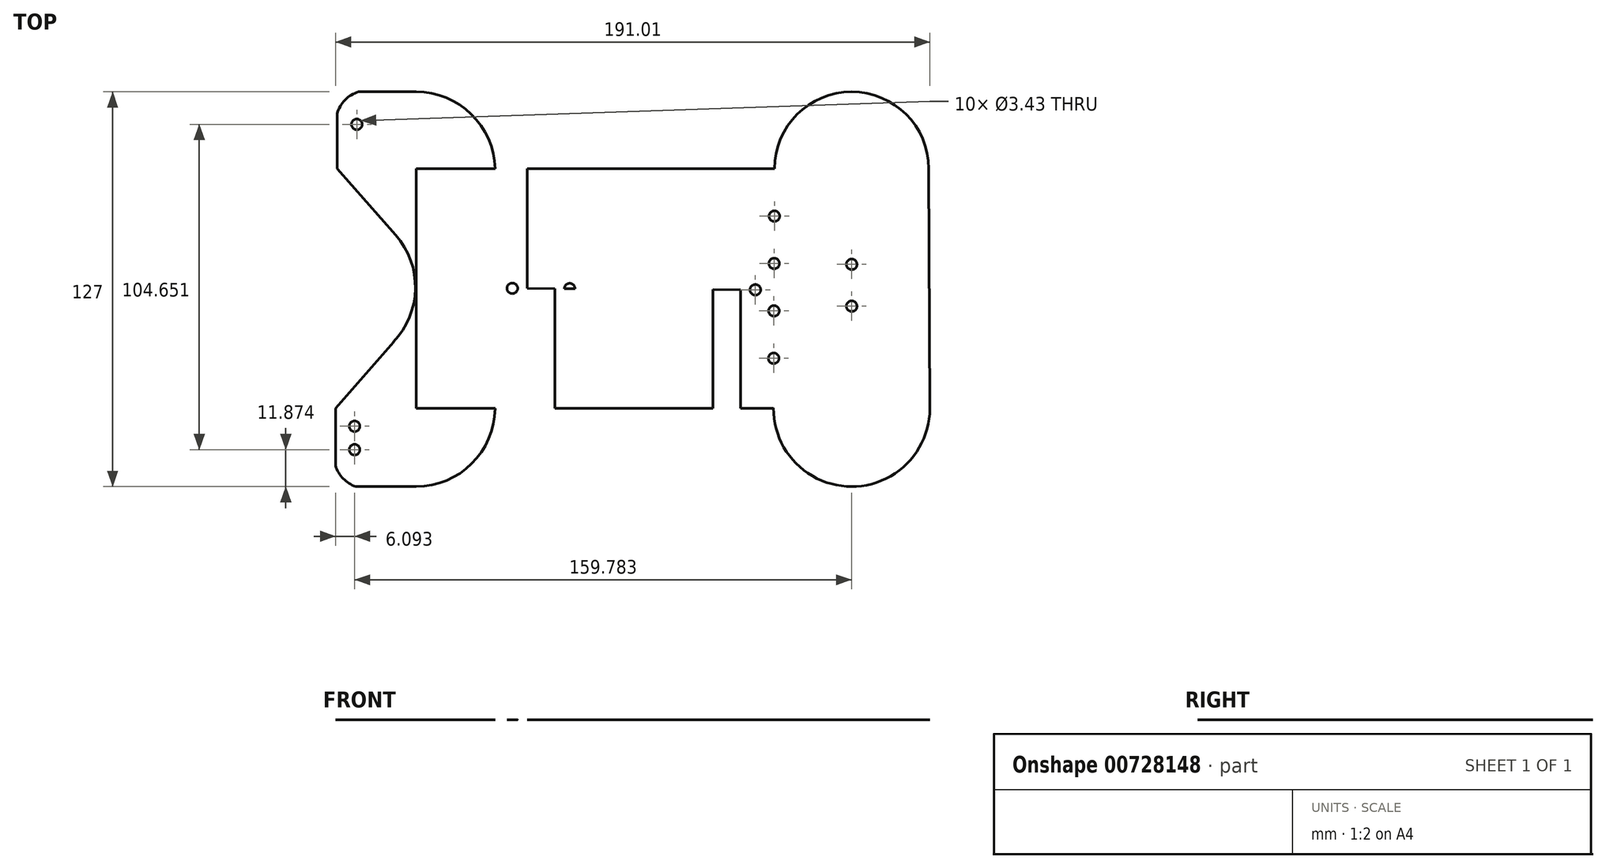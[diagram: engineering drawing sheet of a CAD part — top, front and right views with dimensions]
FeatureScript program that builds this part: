
annotation { "Feature Type Name" : "Feature", "Feature Type Description" : "" }
export const myFeature = defineFeature(function(context is Context, id is Id, definition is map)
    precondition{}
    {
        {
            var Q0;
            Q0=qCreatedBy(makeId("Top.planeOp"),FACE);
            var sketch = newSketch(context, id + "F0", { "sketchPlane" : qUnion([Q0])});
            skLineSegment(sketch, "E0", {"start": v(-83.81, 55.67) * mm, "end": v(-83.81, -21.44) * mm});
            skLineSegment(sketch, "E1", {"start": v(-83.81, 55.67) * mm, "end": v(56.19, 55.67) * mm});
            skCircle(sketch, "E2", {"center": v(56.19, 55.67) * mm, "radius": 24.77 * mm});
            skLineSegment(sketch, "E3", {"start": v(56.19, 55.67) * mm, "end": v(56.19, -21.44) * mm});
            skLineSegment(sketch, "E4", {"start": v(56.19, -21.44) * mm, "end": v(-83.81, -21.44) * mm});
            skCircle(sketch, "E5", {"center": v(56.19, -21.44) * mm, "radius": 25.13 * mm});
            skLineSegment(sketch, "E6", {"start": v(-83.81, 55.67) * mm, "end": v(-83.81, 80.43) * mm});
            skLineSegment(sketch, "E7", {"start": v(-83.81, -21.44) * mm, "end": v(-83.81, -46.57) * mm});
            skLineSegment(sketch, "E8", {"start": v(-83.81, 55.67) * mm, "end": v(-109.21, 55.67) * mm});
            skLineSegment(sketch, "E9", {"start": v(-83.81, -21.44) * mm, "end": v(-109.7, -21.44) * mm});
            skLineSegment(sketch, "E10", {"start": v(56.19, 55.67) * mm, "end": v(56.19, 80.43) * mm});
            skLineSegment(sketch, "E11", {"start": v(56.19, 55.67) * mm, "end": v(80.95, 55.67) * mm});
            skLineSegment(sketch, "E12", {"start": v(56.19, -21.44) * mm, "end": v(81.32, -21.44) * mm});
            skLineSegment(sketch, "E13", {"start": v(56.19, -21.44) * mm, "end": v(56.19, -46.57) * mm});
            skLineSegment(sketch, "E14", {"start": v(-109.21, 55.67) * mm, "end": v(-109.7, -21.44) * mm});
            skLineSegment(sketch, "E15", {"start": v(-83.81, 80.43) * mm, "end": v(56.19, 80.43) * mm});
            skLineSegment(sketch, "E16", {"start": v(80.95, 55.67) * mm, "end": v(81.32, -21.44) * mm});
            skLineSegment(sketch, "E17", {"start": v(-83.81, -46.57) * mm, "end": v(56.19, -46.57) * mm});
            skLineSegment(sketch, "E18", {"start": v(-51.92, 55.67) * mm, "end": v(24.28, 55.67) * mm});
            skLineSegment(sketch, "E19", {"start": v(-51.92, 55.67) * mm, "end": v(-58.42, 55.67) * mm});
            skLineSegment(sketch, "E20", {"start": v(-48.1, 55.67) * mm, "end": v(20.47, 55.67) * mm});
            skLineSegment(sketch, "E21.bottom", {"start": v(-48.1, 55.67) * mm, "end": v(-39.22, 55.67) * mm});
            skLineSegment(sketch, "E21.top", {"start": v(-48.1, -21.44) * mm, "end": v(-39.22, -21.44) * mm});
            skLineSegment(sketch, "E21.left", {"start": v(-48.1, 55.67) * mm, "end": v(-48.1, -21.44) * mm});
            skLineSegment(sketch, "E21.right", {"start": v(-39.22, 55.67) * mm, "end": v(-39.22, -21.44) * mm});
            skLineSegment(sketch, "E22.bottom", {"start": v(20.47, 55.67) * mm, "end": v(11.58, 55.67) * mm});
            skLineSegment(sketch, "E22.top", {"start": v(20.47, -21.44) * mm, "end": v(11.58, -21.44) * mm});
            skLineSegment(sketch, "E22.left", {"start": v(20.47, 55.67) * mm, "end": v(20.47, -21.44) * mm});
            skLineSegment(sketch, "E22.right", {"start": v(11.58, 55.67) * mm, "end": v(11.58, -21.44) * mm});
            skLineSegment(sketch, "E23", {"start": v(-109.45, 17.57) * mm, "end": v(81.14, 16.38) * mm});
            skCircle(sketch, "E24", {"center": v(-52.88, 17.22) * mm, "radius": 1.71 * mm});
            skCircle(sketch, "E25", {"center": v(-34.44, 17.1) * mm, "radius": 1.71 * mm});
            skCircle(sketch, "E26", {"center": v(6.8, 16.84) * mm, "radius": 1.71 * mm});
            skCircle(sketch, "E27", {"center": v(25.23, 16.73) * mm, "radius": 1.71 * mm});
            skLineSegment(sketch, "E28", {"start": v(56.19, 30.9) * mm, "end": v(56.19, 3.7) * mm});
            skCircle(sketch, "E29", {"center": v(56.19, 24.93) * mm, "radius": 1.71 * mm});
            skCircle(sketch, "E30", {"center": v(56.19, 11.47) * mm, "radius": 1.71 * mm});
            skCircle(sketch, "E31", {"center": v(-109.45, 17.57) * mm, "radius": 25.4 * mm});
            skLineSegment(sketch, "E32", {"start": v(-109.21, 55.67) * mm, "end": v(-90.41, 34.38) * mm});
            skLineSegment(sketch, "E33", {"start": v(-109.7, -21.44) * mm, "end": v(-91.07, 0) * mm});
            skLineSegment(sketch, "E34", {"start": v(-96.51, 55.67) * mm, "end": v(-102.86, 55.67) * mm});
            skLineSegment(sketch, "E35.bottom", {"start": v(-109.7, -21.44) * mm, "end": v(-83.81, -21.44) * mm});
            skLineSegment(sketch, "E35.top", {"start": v(-109.7, -46.57) * mm, "end": v(-83.81, -46.57) * mm});
            skLineSegment(sketch, "E35.left", {"start": v(-109.7, -21.44) * mm, "end": v(-109.7, -46.57) * mm});
            skLineSegment(sketch, "E36.bottom", {"start": v(-83.81, 80.43) * mm, "end": v(-109.21, 80.43) * mm});
            skLineSegment(sketch, "E36.left", {"start": v(-83.81, 80.43) * mm, "end": v(-83.81, 55.67) * mm});
            skLineSegment(sketch, "E36.right", {"start": v(-109.21, 80.43) * mm, "end": v(-109.21, 55.67) * mm});
            skArc(sketch, "E37", {"start": v(-96.51, 80.43) * mm, "mid": v(-106.5, 77.97) * mm, "end": v(-109.21, 68.05) * mm});
            skArc(sketch, "E38", {"start": v(-109.7, -34) * mm, "mid": v(-107.04, -44.22) * mm, "end": v(-96.75, -46.57) * mm});
            skLineSegment(sketch, "E39", {"start": v(-109.21, 55.67) * mm, "end": v(-99.69, 55.67) * mm});
            skLineSegment(sketch, "E40.bottom", {"start": v(-99.69, 55.67) * mm, "end": v(-109.21, 55.67) * mm});
            skLineSegment(sketch, "E40.top", {"start": v(-99.69, 74.72) * mm, "end": v(-109.21, 74.72) * mm});
            skLineSegment(sketch, "E40.left", {"start": v(-99.69, 55.67) * mm, "end": v(-99.69, 74.72) * mm});
            skLineSegment(sketch, "E40.right", {"start": v(-109.21, 55.67) * mm, "end": v(-109.21, 74.72) * mm});
            skArc(sketch, "E41", {"start": v(-58.42, 55.67) * mm, "mid": v(-66.08, 73.22) * mm, "end": v(-83.81, 80.43) * mm});
            skLineSegment(sketch, "E42", {"start": v(-83.81, -21.44) * mm, "end": v(-58.41, -21.44) * mm});
            skLineSegment(sketch, "E43", {"start": v(-58.41, -21.44) * mm, "end": v(-58.41, -46.57) * mm});
            skArc(sketch, "E44", {"start": v(-83.81, -46.57) * mm, "mid": v(-65.95, -39.22) * mm, "end": v(-58.41, -21.44) * mm});
            skLineSegment(sketch, "E45", {"start": v(-102.86, 74.72) * mm, "end": v(-102.86, 55.67) * mm});
            skCircle(sketch, "E46", {"center": v(-102.86, 69.96) * mm, "radius": 1.71 * mm});
            skCircle(sketch, "E47", {"center": v(-102.86, 60.43) * mm, "radius": 1.71 * mm});
            skLineSegment(sketch, "E48.bottom", {"start": v(-100.17, -21.44) * mm, "end": v(-109.7, -21.44) * mm});
            skLineSegment(sketch, "E48.top", {"start": v(-100.17, -40.49) * mm, "end": v(-109.7, -40.49) * mm});
            skLineSegment(sketch, "E48.left", {"start": v(-100.17, -21.44) * mm, "end": v(-100.17, -40.49) * mm});
            skLineSegment(sketch, "E48.right", {"start": v(-109.7, -21.44) * mm, "end": v(-109.7, -40.49) * mm});
            skLineSegment(sketch, "E49", {"start": v(-103.6, -21.44) * mm, "end": v(-103.6, -40.49) * mm});
            skCircle(sketch, "E50", {"center": v(-103.6, -27.16) * mm, "radius": 1.71 * mm});
            skCircle(sketch, "E51", {"center": v(-103.6, -34.7) * mm, "radius": 1.71 * mm});
            skLineSegment(sketch, "E52", {"start": v(-109.6, -7.83) * mm, "end": v(-109.7, -21.44) * mm});
            skLineSegment(sketch, "E53", {"start": v(-109.6, -7.83) * mm, "end": v(-91.07, 0) * mm});
            skLineSegment(sketch, "E54", {"start": v(31.42, 55.67) * mm, "end": v(31.06, -21.44) * mm});
            skCircle(sketch, "E55", {"center": v(31.35, 40.43) * mm, "radius": 1.71 * mm});
            skCircle(sketch, "E56", {"center": v(31.28, 25.19) * mm, "radius": 1.71 * mm});
            skCircle(sketch, "E57", {"center": v(31.2, 9.95) * mm, "radius": 1.71 * mm});
            skLineSegment(sketch, "E58", {"start": v(31.35, 40.43) * mm, "end": v(31.42, 55.67) * mm});
            skCircle(sketch, "E59", {"center": v(31.13, -5.3) * mm, "radius": 1.71 * mm});
            skSolve(sketch);
        }
        {
            var Q0;
            {var subQ0=sQuery(id+"F0.wireOp",EDGE,"6wYKrSfj-Jo59-tIdZ-Ksw8-WNReIWJIrDqb");var subQ1=sQuery(id+"F0.wireOp",EDGE,"E0");var subQ2=makeQuery(id+"F0.imprint","INTERSECT",VERTEX,{"derivedFrom":[subQ1,subQ0]});Q0=makeQuery(id+"F0.imprint","IMPRINT",FACE,{"disambiguationData":[TD([[makeQuery(id+"F0.imprint","IMPRINT",EDGE,{"disambiguationData":[TD([[subQ2,-1.0]])],"derivedFrom":subQ0}),-1.0]])]});}
            var Q1;
            {var subQ0=sQuery(id+"F0.wireOp",EDGE,"E6");Q1=makeQuery(id+"F0.imprint","IMPRINT",FACE,{"disambiguationData":[TD([[makeQuery(id+"F0.imprint","IMPRINT",EDGE,{"derivedFrom":subQ0}),1.0]])]});}
            var Q2;
            {var subQ1=sQuery(id+"F0.wireOp",EDGE,"KSh8FWiv-c9sq-w0e5-FnnW-knMpXcfZ88Ok");var subQ3=sQuery(id+"F0.wireOp",EDGE,"E0");var subQ4=makeQuery(id+"F0.imprint","INTERSECT",VERTEX,{"derivedFrom":[subQ1,subQ3]});Q2=makeQuery(id+"F0.imprint","IMPRINT",FACE,{"disambiguationData":[TD([[makeQuery(id+"F0.imprint","IMPRINT",EDGE,{"disambiguationData":[TD([[subQ4,-1.0]])],"derivedFrom":subQ1}),1.0]])]});}
            var Q3;
            {var subQ0=sQuery(id+"F0.wireOp",EDGE,"E8");Q3=makeQuery(id+"F0.imprint","IMPRINT",FACE,{"disambiguationData":[TD([[makeQuery(id+"F0.imprint","IMPRINT",EDGE,{"derivedFrom":subQ0}),1.0]])]});}
            var Q4;
            {var subQ4=sQuery(id+"F0.wireOp",EDGE,"E9");Q4=makeQuery(id+"F0.imprint","IMPRINT",FACE,{"disambiguationData":[TD([[makeQuery(id+"F0.imprint","IMPRINT",EDGE,{"derivedFrom":subQ4}),-1.0]])]});}
            var Q5;
            {var subQ0=sQuery(id+"F0.wireOp",EDGE,"E7");Q5=makeQuery(id+"F0.imprint","IMPRINT",FACE,{"disambiguationData":[TD([[makeQuery(id+"F0.imprint","IMPRINT",EDGE,{"derivedFrom":subQ0}),-1.0]])]});}
            var Q6;
            {var subQ1=sQuery(id+"F0.wireOp",EDGE,"E0");var subQ3=sQuery(id+"F0.wireOp",EDGE,"6wYKrSfj-Jo59-tIdZ-Ksw8-WNReIWJIrDqb");var subQ4=makeQuery(id+"F0.imprint","INTERSECT",VERTEX,{"derivedFrom":[subQ1,subQ3]});Q6=makeQuery(id+"F0.imprint","IMPRINT",FACE,{"disambiguationData":[TD([[makeQuery(id+"F0.imprint","IMPRINT",EDGE,{"disambiguationData":[TD([[subQ4,1.0]])],"derivedFrom":subQ3}),1.0]])]});}
            var Q7;
            {var subQ0=sQuery(id+"F0.wireOp",EDGE,"E19");Q7=makeQuery(id+"F0.imprint","IMPRINT",FACE,{"disambiguationData":[TD([[makeQuery(id+"F0.imprint","IMPRINT",EDGE,{"derivedFrom":subQ0}),1.0]])]});}
            var Q8;
            {var subQ0=sQuery(id+"F0.wireOp",EDGE,"E10");Q8=makeQuery(id+"F0.imprint","IMPRINT",FACE,{"disambiguationData":[TD([[makeQuery(id+"F0.imprint","IMPRINT",EDGE,{"derivedFrom":subQ0}),-1.0]])]});}
            var Q9;
            {var subQ0=sQuery(id+"F0.wireOp",EDGE,"E11");Q9=makeQuery(id+"F0.imprint","IMPRINT",FACE,{"disambiguationData":[TD([[makeQuery(id+"F0.imprint","IMPRINT",EDGE,{"derivedFrom":subQ0}),-1.0]])]});}
            var Q10;
            {var subQ5=sQuery(id+"F0.wireOp",EDGE,"E23");var subQ6=sQuery(id+"F0.wireOp",EDGE,"E16");var subQ7=makeQuery(id+"F0.imprint","INTERSECT",VERTEX,{"derivedFrom":[subQ6,subQ5]});Q10=makeQuery(id+"F0.imprint","IMPRINT",FACE,{"disambiguationData":[TD([[makeQuery(id+"F0.imprint","IMPRINT",EDGE,{"disambiguationData":[TD([[subQ7,1.0]])],"derivedFrom":subQ5}),1.0]])]});}
            var Q11;
            {var subQ1=sQuery(id+"F0.wireOp",EDGE,"E23");var subQ5=sQuery(id+"F0.wireOp",EDGE,"E16");var subQ9=makeQuery(id+"F0.imprint","INTERSECT",VERTEX,{"derivedFrom":[subQ5,subQ1]});Q11=makeQuery(id+"F0.imprint","IMPRINT",FACE,{"disambiguationData":[TD([[makeQuery(id+"F0.imprint","IMPRINT",EDGE,{"disambiguationData":[TD([[subQ9,1.0]])],"derivedFrom":subQ1}),-1.0]])]});}
            var Q12;
            {var subQ0=sQuery(id+"F0.wireOp",EDGE,"E12");Q12=makeQuery(id+"F0.imprint","IMPRINT",FACE,{"disambiguationData":[TD([[makeQuery(id+"F0.imprint","IMPRINT",EDGE,{"derivedFrom":subQ0}),1.0]])]});}
            var Q13;
            {var subQ0=sQuery(id+"F0.wireOp",EDGE,"E12");Q13=makeQuery(id+"F0.imprint","IMPRINT",FACE,{"disambiguationData":[TD([[makeQuery(id+"F0.imprint","IMPRINT",EDGE,{"derivedFrom":subQ0}),-1.0]])]});}
            var Q14;
            {var subQ0=sQuery(id+"F0.wireOp",EDGE,"E4");var subQ3=sQuery(id+"F0.wireOp",EDGE,"E5");var subQ5=makeQuery(id+"F0.imprint","INTERSECT",VERTEX,{"derivedFrom":[subQ0,subQ3]});Q14=makeQuery(id+"F0.imprint","IMPRINT",FACE,{"disambiguationData":[TD([[makeQuery(id+"F0.imprint","IMPRINT",EDGE,{"disambiguationData":[TD([[subQ5,1.0]])],"derivedFrom":subQ3}),1.0]])]});}
            var Q15;
            {var subQ0=sQuery(id+"F0.wireOp",EDGE,"E6");Q15=makeQuery(id+"F0.imprint","IMPRINT",FACE,{"disambiguationData":[TD([[makeQuery(id+"F0.imprint","IMPRINT",EDGE,{"derivedFrom":subQ0}),-1.0]])]});}
            var Q16;
            {var subQ0=sQuery(id+"F0.wireOp",EDGE,"E7");Q16=makeQuery(id+"F0.imprint","IMPRINT",FACE,{"disambiguationData":[TD([[makeQuery(id+"F0.imprint","IMPRINT",EDGE,{"derivedFrom":subQ0}),1.0]])]});}
            var Q17;
            {var subQ6=sQuery(id+"F0.wireOp",EDGE,"E20");Q17=makeQuery(id+"F0.imprint","IMPRINT",FACE,{"disambiguationData":[TD([[makeQuery(id+"F0.imprint","IMPRINT",EDGE,{"derivedFrom":subQ6}),-1.0]])]});}
            var Q18;
            {var subQ0=sQuery(id+"F0.wireOp",EDGE,"E21.bottom");Q18=makeQuery(id+"F0.imprint","IMPRINT",FACE,{"disambiguationData":[TD([[makeQuery(id+"F0.imprint","IMPRINT",EDGE,{"derivedFrom":subQ0}),-1.0]])]});}
            var Q19;
            {var subQ6=sQuery(id+"F0.wireOp",EDGE,"6wYKrSfj-Jo59-tIdZ-Ksw8-WNReIWJIrDqb");var subQ7=sQuery(id+"F0.wireOp",EDGE,"E0");var subQ8=makeQuery(id+"F0.imprint","INTERSECT",VERTEX,{"derivedFrom":[subQ7,subQ6]});Q19=makeQuery(id+"F0.imprint","IMPRINT",FACE,{"disambiguationData":[TD([[makeQuery(id+"F0.imprint","IMPRINT",EDGE,{"disambiguationData":[TD([[subQ8,1.0]])],"derivedFrom":subQ6}),-1.0]])]});}
            var Q20;
            {var subQ0=sQuery(id+"F0.wireOp",EDGE,"E21.top");Q20=makeQuery(id+"F0.imprint","IMPRINT",FACE,{"disambiguationData":[TD([[makeQuery(id+"F0.imprint","IMPRINT",EDGE,{"derivedFrom":subQ0}),1.0]])]});}
            var Q21;
            {var subQ0=sQuery(id+"F0.wireOp",EDGE,"E22.top");Q21=makeQuery(id+"F0.imprint","IMPRINT",FACE,{"disambiguationData":[TD([[makeQuery(id+"F0.imprint","IMPRINT",EDGE,{"derivedFrom":subQ0}),-1.0]])]});}
            var Q22;
            {var subQ0=sQuery(id+"F0.wireOp",EDGE,"E22.bottom");Q22=makeQuery(id+"F0.imprint","IMPRINT",FACE,{"disambiguationData":[TD([[makeQuery(id+"F0.imprint","IMPRINT",EDGE,{"derivedFrom":subQ0}),1.0]])]});}
            var Q23;
            {var subQ1=sQuery(id+"F0.wireOp",EDGE,"E1");var subQ3=sQuery(id+"F0.wireOp",EDGE,"E2");var subQ4=makeQuery(id+"F0.imprint","INTERSECT",VERTEX,{"derivedFrom":[subQ1,subQ3]});Q23=makeQuery(id+"F0.imprint","IMPRINT",FACE,{"disambiguationData":[TD([[makeQuery(id+"F0.imprint","IMPRINT",EDGE,{"disambiguationData":[TD([[subQ4,-1.0]])],"derivedFrom":subQ3}),1.0]])]});}
            var Q24;
            {var subQ1=sQuery(id+"F0.wireOp",EDGE,"E18");var subQ6=sQuery(id+"F0.wireOp",EDGE,"E1");var subQ7=makeQuery(id+"F0.imprint","INTERSECT",VERTEX,{"derivedFrom":[subQ6,subQ1]});Q24=makeQuery(id+"F0.imprint","IMPRINT",FACE,{"disambiguationData":[TD([[makeQuery(id+"F0.imprint","IMPRINT",EDGE,{"disambiguationData":[TD([[subQ7,-1.0]])],"derivedFrom":subQ6}),-1.0]])]});}
            var Q25;
            {var subQ0=sQuery(id+"F0.wireOp",EDGE,"E31");var subQ1=sQuery(id+"F0.wireOp",EDGE,"KSh8FWiv-c9sq-w0e5-FnnW-knMpXcfZ88Ok");var subQ2=makeQuery(id+"F0.imprint","INTERSECT",VERTEX,{"disambiguationData":[OD(1.0)],"derivedFrom":[subQ1,subQ0]});Q25=makeQuery(id+"F0.imprint","IMPRINT",FACE,{"disambiguationData":[TD([[makeQuery(id+"F0.imprint","IMPRINT",EDGE,{"disambiguationData":[TD([[subQ2,-1.0]])],"derivedFrom":subQ1}),-1.0]])]});}
            var Q26;
            {var subQ0=sQuery(id+"F0.wireOp",EDGE,"E32");Q26=makeQuery(id+"F0.imprint","IMPRINT",FACE,{"disambiguationData":[TD([[makeQuery(id+"F0.imprint","IMPRINT",EDGE,{"derivedFrom":subQ0}),1.0]])]});}
            var Q27;
            {var subQ3=sQuery(id+"F0.wireOp",EDGE,"E36.left");Q27=makeQuery(id+"F0.imprint","IMPRINT",FACE,{"disambiguationData":[TD([[makeQuery(id+"F0.imprint","IMPRINT",EDGE,{"derivedFrom":subQ3}),-1.0]])]});}
            var Q28;
            {var subQ6=sQuery(id+"F0.wireOp",EDGE,"WmSTnMDh-z46E-Ozi7-dlK6-xB8Bdzc5yjVP");Q28=makeQuery(id+"F0.imprint","IMPRINT",FACE,{"disambiguationData":[TD([[makeQuery(id+"F0.imprint","IMPRINT",EDGE,{"derivedFrom":subQ6}),-1.0]])]});}
            var Q29;
            {var subQ1=sQuery(id+"F0.wireOp",EDGE,"WmSTnMDh-z46E-Ozi7-dlK6-xB8Bdzc5yjVP");Q29=makeQuery(id+"F0.imprint","IMPRINT",FACE,{"disambiguationData":[TD([[makeQuery(id+"F0.imprint","IMPRINT",EDGE,{"derivedFrom":subQ1}),1.0]])]});}
            var Q30;
            {var subQ0=sQuery(id+"F0.wireOp",EDGE,"E33");Q30=makeQuery(id+"F0.imprint","IMPRINT",FACE,{"disambiguationData":[TD([[makeQuery(id+"F0.imprint","IMPRINT",EDGE,{"derivedFrom":subQ0}),-1.0]])]});}
            var Q31;
            {var subQ6=sQuery(id+"F0.wireOp",EDGE,"E7");Q31=makeQuery(id+"F0.imprint","IMPRINT",FACE,{"disambiguationData":[TD([[makeQuery(id+"F0.imprint","IMPRINT",EDGE,{"derivedFrom":subQ6}),-1.0]])]});}
            var Q32;
            {var subQ6=sQuery(id+"F0.wireOp",EDGE,"OAJegEEa-Hw3k-cZKG-yG8Y-cdVKGBYDG2lV");Q32=makeQuery(id+"F0.imprint","IMPRINT",FACE,{"disambiguationData":[TD([[makeQuery(id+"F0.imprint","IMPRINT",EDGE,{"derivedFrom":subQ6}),1.0]])]});}
            var Q33;
            {var subQ1=sQuery(id+"F0.wireOp",EDGE,"OAJegEEa-Hw3k-cZKG-yG8Y-cdVKGBYDG2lV");Q33=makeQuery(id+"F0.imprint","IMPRINT",FACE,{"disambiguationData":[TD([[makeQuery(id+"F0.imprint","IMPRINT",EDGE,{"derivedFrom":subQ1}),-1.0]])]});}
            var Q34;
            {var subQ5=sQuery(id+"F0.wireOp",EDGE,"E42");Q34=makeQuery(id+"F0.imprint","IMPRINT",FACE,{"disambiguationData":[TD([[makeQuery(id+"F0.imprint","IMPRINT",EDGE,{"derivedFrom":subQ5}),1.0]])]});}
            var Q35;
            {var subQ0=sQuery(id+"F0.wireOp",EDGE,"E40.left");Q35=makeQuery(id+"F0.imprint","IMPRINT",FACE,{"disambiguationData":[TD([[makeQuery(id+"F0.imprint","IMPRINT",EDGE,{"derivedFrom":subQ0}),1.0]])]});}
            var Q36;
            {var subQ3=sQuery(id+"F0.wireOp",EDGE,"E37");var subQ7=sQuery(id+"F0.wireOp",EDGE,"E40.right");var subQ12=makeQuery(id+"F0.imprint","INTERSECT",VERTEX,{"disambiguationData":[OD(1.0)],"derivedFrom":[subQ3,subQ7]});Q36=makeQuery(id+"F0.imprint","IMPRINT",FACE,{"disambiguationData":[TD([[makeQuery(id+"F0.imprint","IMPRINT",EDGE,{"disambiguationData":[TD([[subQ12,1.0]])],"derivedFrom":subQ3}),1.0]])]});}
            var Q37;
            {var subQ3=sQuery(id+"F0.wireOp",EDGE,"E38");var subQ8=sQuery(id+"F0.wireOp",EDGE,"E48.right");var subQ13=makeQuery(id+"F0.imprint","INTERSECT",VERTEX,{"disambiguationData":[OD(1.0)],"derivedFrom":[subQ3,subQ8]});Q37=makeQuery(id+"F0.imprint","IMPRINT",FACE,{"disambiguationData":[TD([[makeQuery(id+"F0.imprint","IMPRINT",EDGE,{"disambiguationData":[TD([[subQ13,-1.0]])],"derivedFrom":subQ3}),1.0]])]});}
            var Q38;
            {var subQ3=sQuery(id+"F0.wireOp",EDGE,"E23");var subQ5=sQuery(id+"F0.wireOp",EDGE,"E25");var subQ6=makeQuery(id+"F0.imprint","INTERSECT",VERTEX,{"disambiguationData":[OD(1.0)],"derivedFrom":[subQ3,subQ5]});Q38=makeQuery(id+"F0.imprint","IMPRINT",FACE,{"disambiguationData":[TD([[makeQuery(id+"F0.imprint","IMPRINT",EDGE,{"disambiguationData":[TD([[subQ6,-1.0]])],"derivedFrom":subQ3}),-1.0]])]});}
            var Q39;
            {var subQ0=sQuery(id+"F0.wireOp",EDGE,"E23");var subQ1=sQuery(id+"F0.wireOp",EDGE,"E22.left");var subQ2=makeQuery(id+"F0.imprint","INTERSECT",VERTEX,{"derivedFrom":[subQ1,subQ0]});Q39=makeQuery(id+"F0.imprint","IMPRINT",FACE,{"disambiguationData":[TD([[makeQuery(id+"F0.imprint","IMPRINT",EDGE,{"disambiguationData":[TD([[subQ2,-1.0]])],"derivedFrom":subQ0}),-1.0]])]});}
            var Q40;
            {var subQ10=sQuery(id+"F0.wireOp",EDGE,"E35.bottom");Q40=makeQuery(id+"F0.imprint","IMPRINT",FACE,{"disambiguationData":[TD([[makeQuery(id+"F0.imprint","IMPRINT",EDGE,{"derivedFrom":subQ10}),1.0]])]});}
            var Q41;
            {var subQ9=sQuery(id+"F0.wireOp",EDGE,"E23");var subQ12=sQuery(id+"F0.wireOp",EDGE,"E54");var subQ13=makeQuery(id+"F0.imprint","INTERSECT",VERTEX,{"derivedFrom":[subQ9,subQ12]});Q41=makeQuery(id+"F0.imprint","IMPRINT",FACE,{"disambiguationData":[TD([[makeQuery(id+"F0.imprint","IMPRINT",EDGE,{"disambiguationData":[TD([[subQ13,-1.0]])],"derivedFrom":subQ9}),1.0]])]});}
            var Q42;
            {var subQ5=sQuery(id+"F0.wireOp",EDGE,"E23");var subQ8=sQuery(id+"F0.wireOp",EDGE,"E54");var subQ9=makeQuery(id+"F0.imprint","INTERSECT",VERTEX,{"derivedFrom":[subQ5,subQ8]});Q42=makeQuery(id+"F0.imprint","IMPRINT",FACE,{"disambiguationData":[TD([[makeQuery(id+"F0.imprint","IMPRINT",EDGE,{"disambiguationData":[TD([[subQ9,-1.0]])],"derivedFrom":subQ5}),-1.0]])]});}
            var Q43;
            {var subQ0=sQuery(id+"F0.wireOp",EDGE,"E24");var subQ1=sQuery(id+"F0.wireOp",EDGE,"E23");var subQ2=makeQuery(id+"F0.imprint","INTERSECT",VERTEX,{"disambiguationData":[OD(0.0)],"derivedFrom":[subQ1,subQ0]});Q43=makeQuery(id+"F0.imprint","IMPRINT",FACE,{"disambiguationData":[TD([[makeQuery(id+"F0.imprint","IMPRINT",EDGE,{"disambiguationData":[TD([[subQ2,-1.0]])],"derivedFrom":subQ1}),-1.0]])]});}
            var Q44;
            {var subQ0=sQuery(id+"F0.wireOp",EDGE,"E24");var subQ1=sQuery(id+"F0.wireOp",EDGE,"E23");var subQ2=makeQuery(id+"F0.imprint","INTERSECT",VERTEX,{"disambiguationData":[OD(0.0)],"derivedFrom":[subQ1,subQ0]});Q44=makeQuery(id+"F0.imprint","IMPRINT",FACE,{"disambiguationData":[TD([[makeQuery(id+"F0.imprint","IMPRINT",EDGE,{"disambiguationData":[TD([[subQ2,-1.0]])],"derivedFrom":subQ1}),1.0]])]});}
            var Q45;
            {var subQ0=sQuery(id+"F0.wireOp",EDGE,"E25");var subQ1=sQuery(id+"F0.wireOp",EDGE,"E23");var subQ2=makeQuery(id+"F0.imprint","INTERSECT",VERTEX,{"disambiguationData":[OD(0.0)],"derivedFrom":[subQ1,subQ0]});Q45=makeQuery(id+"F0.imprint","IMPRINT",FACE,{"disambiguationData":[TD([[makeQuery(id+"F0.imprint","IMPRINT",EDGE,{"disambiguationData":[TD([[subQ2,-1.0]])],"derivedFrom":subQ1}),-1.0]])]});}
            var Q46;
            {var subQ0=sQuery(id+"F0.wireOp",EDGE,"E25");var subQ1=sQuery(id+"F0.wireOp",EDGE,"E23");var subQ2=makeQuery(id+"F0.imprint","INTERSECT",VERTEX,{"disambiguationData":[OD(0.0)],"derivedFrom":[subQ1,subQ0]});Q46=makeQuery(id+"F0.imprint","IMPRINT",FACE,{"disambiguationData":[TD([[makeQuery(id+"F0.imprint","IMPRINT",EDGE,{"disambiguationData":[TD([[subQ2,-1.0]])],"derivedFrom":subQ1}),1.0]])]});}
            var Q47;
            {var subQ0=sQuery(id+"F0.wireOp",EDGE,"E26");var subQ1=sQuery(id+"F0.wireOp",EDGE,"E23");var subQ2=makeQuery(id+"F0.imprint","INTERSECT",VERTEX,{"disambiguationData":[OD(0.0)],"derivedFrom":[subQ1,subQ0]});Q47=makeQuery(id+"F0.imprint","IMPRINT",FACE,{"disambiguationData":[TD([[makeQuery(id+"F0.imprint","IMPRINT",EDGE,{"disambiguationData":[TD([[subQ2,-1.0]])],"derivedFrom":subQ1}),-1.0]])]});}
            var Q48;
            {var subQ0=sQuery(id+"F0.wireOp",EDGE,"E26");var subQ1=sQuery(id+"F0.wireOp",EDGE,"E23");var subQ2=makeQuery(id+"F0.imprint","INTERSECT",VERTEX,{"disambiguationData":[OD(0.0)],"derivedFrom":[subQ1,subQ0]});Q48=makeQuery(id+"F0.imprint","IMPRINT",FACE,{"disambiguationData":[TD([[makeQuery(id+"F0.imprint","IMPRINT",EDGE,{"disambiguationData":[TD([[subQ2,-1.0]])],"derivedFrom":subQ1}),1.0]])]});}
            var Q49;
            {var subQ0=sQuery(id+"F0.wireOp",EDGE,"E27");var subQ1=sQuery(id+"F0.wireOp",EDGE,"E23");var subQ2=makeQuery(id+"F0.imprint","INTERSECT",VERTEX,{"disambiguationData":[OD(0.0)],"derivedFrom":[subQ1,subQ0]});Q49=makeQuery(id+"F0.imprint","IMPRINT",FACE,{"disambiguationData":[TD([[makeQuery(id+"F0.imprint","IMPRINT",EDGE,{"disambiguationData":[TD([[subQ2,-1.0]])],"derivedFrom":subQ1}),-1.0]])]});}
            var Q50;
            {var subQ0=sQuery(id+"F0.wireOp",EDGE,"E27");var subQ1=sQuery(id+"F0.wireOp",EDGE,"E23");var subQ2=makeQuery(id+"F0.imprint","INTERSECT",VERTEX,{"disambiguationData":[OD(0.0)],"derivedFrom":[subQ1,subQ0]});Q50=makeQuery(id+"F0.imprint","IMPRINT",FACE,{"disambiguationData":[TD([[makeQuery(id+"F0.imprint","IMPRINT",EDGE,{"disambiguationData":[TD([[subQ2,-1.0]])],"derivedFrom":subQ1}),1.0]])]});}
            var Q51;
            {var subQ0=sQuery(id+"F0.wireOp",EDGE,"E29");var subQ1=sQuery(id+"F0.wireOp",EDGE,"E28");var subQ2=makeQuery(id+"F0.imprint","INTERSECT",VERTEX,{"disambiguationData":[OD(0.0)],"derivedFrom":[subQ1,subQ0]});Q51=makeQuery(id+"F0.imprint","IMPRINT",FACE,{"disambiguationData":[TD([[makeQuery(id+"F0.imprint","IMPRINT",EDGE,{"disambiguationData":[TD([[subQ2,-1.0]])],"derivedFrom":subQ1}),1.0]])]});}
            var Q52;
            {var subQ0=sQuery(id+"F0.wireOp",EDGE,"E30");var subQ1=sQuery(id+"F0.wireOp",EDGE,"E28");var subQ2=makeQuery(id+"F0.imprint","INTERSECT",VERTEX,{"disambiguationData":[OD(0.0)],"derivedFrom":[subQ1,subQ0]});Q52=makeQuery(id+"F0.imprint","IMPRINT",FACE,{"disambiguationData":[TD([[makeQuery(id+"F0.imprint","IMPRINT",EDGE,{"disambiguationData":[TD([[subQ2,-1.0]])],"derivedFrom":subQ1}),1.0]])]});}
            var Q53;
            {var subQ0=sQuery(id+"F0.wireOp",EDGE,"E30");var subQ1=sQuery(id+"F0.wireOp",EDGE,"E28");var subQ2=makeQuery(id+"F0.imprint","INTERSECT",VERTEX,{"disambiguationData":[OD(0.0)],"derivedFrom":[subQ1,subQ0]});Q53=makeQuery(id+"F0.imprint","IMPRINT",FACE,{"disambiguationData":[TD([[makeQuery(id+"F0.imprint","IMPRINT",EDGE,{"disambiguationData":[TD([[subQ2,-1.0]])],"derivedFrom":subQ1}),-1.0]])]});}
            var Q54;
            {var subQ0=sQuery(id+"F0.wireOp",EDGE,"E50");var subQ1=sQuery(id+"F0.wireOp",EDGE,"E49");var subQ2=makeQuery(id+"F0.imprint","INTERSECT",VERTEX,{"disambiguationData":[OD(0.0)],"derivedFrom":[subQ1,subQ0]});Q54=makeQuery(id+"F0.imprint","IMPRINT",FACE,{"disambiguationData":[TD([[makeQuery(id+"F0.imprint","IMPRINT",EDGE,{"disambiguationData":[TD([[subQ2,-1.0]])],"derivedFrom":subQ1}),1.0]])]});}
            var Q55;
            {var subQ0=sQuery(id+"F0.wireOp",EDGE,"E50");var subQ1=sQuery(id+"F0.wireOp",EDGE,"E49");var subQ2=makeQuery(id+"F0.imprint","INTERSECT",VERTEX,{"disambiguationData":[OD(0.0)],"derivedFrom":[subQ1,subQ0]});Q55=makeQuery(id+"F0.imprint","IMPRINT",FACE,{"disambiguationData":[TD([[makeQuery(id+"F0.imprint","IMPRINT",EDGE,{"disambiguationData":[TD([[subQ2,-1.0]])],"derivedFrom":subQ1}),-1.0]])]});}
            var Q56;
            {var subQ0=sQuery(id+"F0.wireOp",EDGE,"E51");var subQ1=sQuery(id+"F0.wireOp",EDGE,"E49");var subQ2=makeQuery(id+"F0.imprint","INTERSECT",VERTEX,{"disambiguationData":[OD(0.0)],"derivedFrom":[subQ1,subQ0]});Q56=makeQuery(id+"F0.imprint","IMPRINT",FACE,{"disambiguationData":[TD([[makeQuery(id+"F0.imprint","IMPRINT",EDGE,{"disambiguationData":[TD([[subQ2,-1.0]])],"derivedFrom":subQ1}),-1.0]])]});}
            var Q57;
            {var subQ5=sQuery(id+"F0.wireOp",EDGE,"E48.left");Q57=makeQuery(id+"F0.imprint","IMPRINT",FACE,{"disambiguationData":[TD([[makeQuery(id+"F0.imprint","IMPRINT",EDGE,{"derivedFrom":subQ5}),-1.0]])]});}
            var Q58;
            {var subQ0=sQuery(id+"F0.wireOp",EDGE,"E51");var subQ1=sQuery(id+"F0.wireOp",EDGE,"E49");var subQ2=makeQuery(id+"F0.imprint","INTERSECT",VERTEX,{"disambiguationData":[OD(0.0)],"derivedFrom":[subQ1,subQ0]});Q58=makeQuery(id+"F0.imprint","IMPRINT",FACE,{"disambiguationData":[TD([[makeQuery(id+"F0.imprint","IMPRINT",EDGE,{"disambiguationData":[TD([[subQ2,-1.0]])],"derivedFrom":subQ1}),1.0]])]});}
            var Q59;
            {var subQ0=sQuery(id+"F0.wireOp",EDGE,"E47");var subQ1=sQuery(id+"F0.wireOp",EDGE,"E45");var subQ2=makeQuery(id+"F0.imprint","INTERSECT",VERTEX,{"disambiguationData":[OD(0.0)],"derivedFrom":[subQ1,subQ0]});Q59=makeQuery(id+"F0.imprint","IMPRINT",FACE,{"disambiguationData":[TD([[makeQuery(id+"F0.imprint","IMPRINT",EDGE,{"disambiguationData":[TD([[subQ2,-1.0]])],"derivedFrom":subQ1}),1.0]])]});}
            var Q60;
            {var subQ0=sQuery(id+"F0.wireOp",EDGE,"E47");var subQ1=sQuery(id+"F0.wireOp",EDGE,"E45");var subQ2=makeQuery(id+"F0.imprint","INTERSECT",VERTEX,{"disambiguationData":[OD(0.0)],"derivedFrom":[subQ1,subQ0]});Q60=makeQuery(id+"F0.imprint","IMPRINT",FACE,{"disambiguationData":[TD([[makeQuery(id+"F0.imprint","IMPRINT",EDGE,{"disambiguationData":[TD([[subQ2,-1.0]])],"derivedFrom":subQ1}),-1.0]])]});}
            var Q61;
            {var subQ0=sQuery(id+"F0.wireOp",EDGE,"E46");var subQ1=sQuery(id+"F0.wireOp",EDGE,"E45");var subQ2=makeQuery(id+"F0.imprint","INTERSECT",VERTEX,{"disambiguationData":[OD(0.0)],"derivedFrom":[subQ1,subQ0]});Q61=makeQuery(id+"F0.imprint","IMPRINT",FACE,{"disambiguationData":[TD([[makeQuery(id+"F0.imprint","IMPRINT",EDGE,{"disambiguationData":[TD([[subQ2,-1.0]])],"derivedFrom":subQ1}),1.0]])]});}
            var Q62;
            {var subQ0=sQuery(id+"F0.wireOp",EDGE,"E46");var subQ1=sQuery(id+"F0.wireOp",EDGE,"E45");var subQ2=makeQuery(id+"F0.imprint","INTERSECT",VERTEX,{"disambiguationData":[OD(0.0)],"derivedFrom":[subQ1,subQ0]});Q62=makeQuery(id+"F0.imprint","IMPRINT",FACE,{"disambiguationData":[TD([[makeQuery(id+"F0.imprint","IMPRINT",EDGE,{"disambiguationData":[TD([[subQ2,-1.0]])],"derivedFrom":subQ1}),-1.0]])]});}
            var Q63;
            {var subQ0=sQuery(id+"F0.wireOp",EDGE,"E29");var subQ1=sQuery(id+"F0.wireOp",EDGE,"E28");var subQ2=makeQuery(id+"F0.imprint","INTERSECT",VERTEX,{"disambiguationData":[OD(0.0)],"derivedFrom":[subQ1,subQ0]});Q63=makeQuery(id+"F0.imprint","IMPRINT",FACE,{"disambiguationData":[TD([[makeQuery(id+"F0.imprint","IMPRINT",EDGE,{"disambiguationData":[TD([[subQ2,-1.0]])],"derivedFrom":subQ1}),-1.0]])]});}
            var Q64;
            {var subQ0=sQuery(id+"F0.wireOp",EDGE,"E7");Q64=makeQuery(id+"F0.imprint","IMPRINT",FACE,{"disambiguationData":[TD([[makeQuery(id+"F0.imprint","IMPRINT",EDGE,{"derivedFrom":subQ0}),1.0]])]});}
            var Q65;
            {var subQ0=sQuery(id+"F0.wireOp",EDGE,"E36.left");Q65=makeQuery(id+"F0.imprint","IMPRINT",FACE,{"disambiguationData":[TD([[makeQuery(id+"F0.imprint","IMPRINT",EDGE,{"derivedFrom":subQ0}),1.0]])]});}
            var Q66;
            {var subQ0=sQuery(id+"F0.wireOp",EDGE,"E10");Q66=makeQuery(id+"F0.imprint","IMPRINT",FACE,{"disambiguationData":[TD([[makeQuery(id+"F0.imprint","IMPRINT",EDGE,{"derivedFrom":subQ0}),1.0]])]});}
            var Q67;
            {var subQ0=sQuery(id+"F0.wireOp",EDGE,"E13");Q67=makeQuery(id+"F0.imprint","IMPRINT",FACE,{"disambiguationData":[TD([[makeQuery(id+"F0.imprint","IMPRINT",EDGE,{"derivedFrom":subQ0}),-1.0]])]});}
            extrude(context, id + "F1", {"entities" : qUnion([Q0, Q1, Q2, Q3, Q4, Q5, Q6, Q7, Q8, Q9, Q10, Q11, Q12, Q13, Q14, Q15, Q16, Q17, Q18, Q19, Q20, Q21, Q22, Q23, Q24, Q25, Q26, Q27, Q28, Q29, Q30, Q31, Q32, Q33, Q34, Q35, Q36, Q37, Q38, Q39, Q40, Q41, Q42, Q43, Q44, Q45, Q46, Q47, Q48, Q49, Q50, Q51, Q52, Q53, Q54, Q55, Q56, Q57, Q58, Q59, Q60, Q61, Q62, Q63, Q64, Q65, Q66, Q67]), "depth" : 1 / 203.2 * mm, "offsetDistance" : 25.4 * mm});
        }
    });
